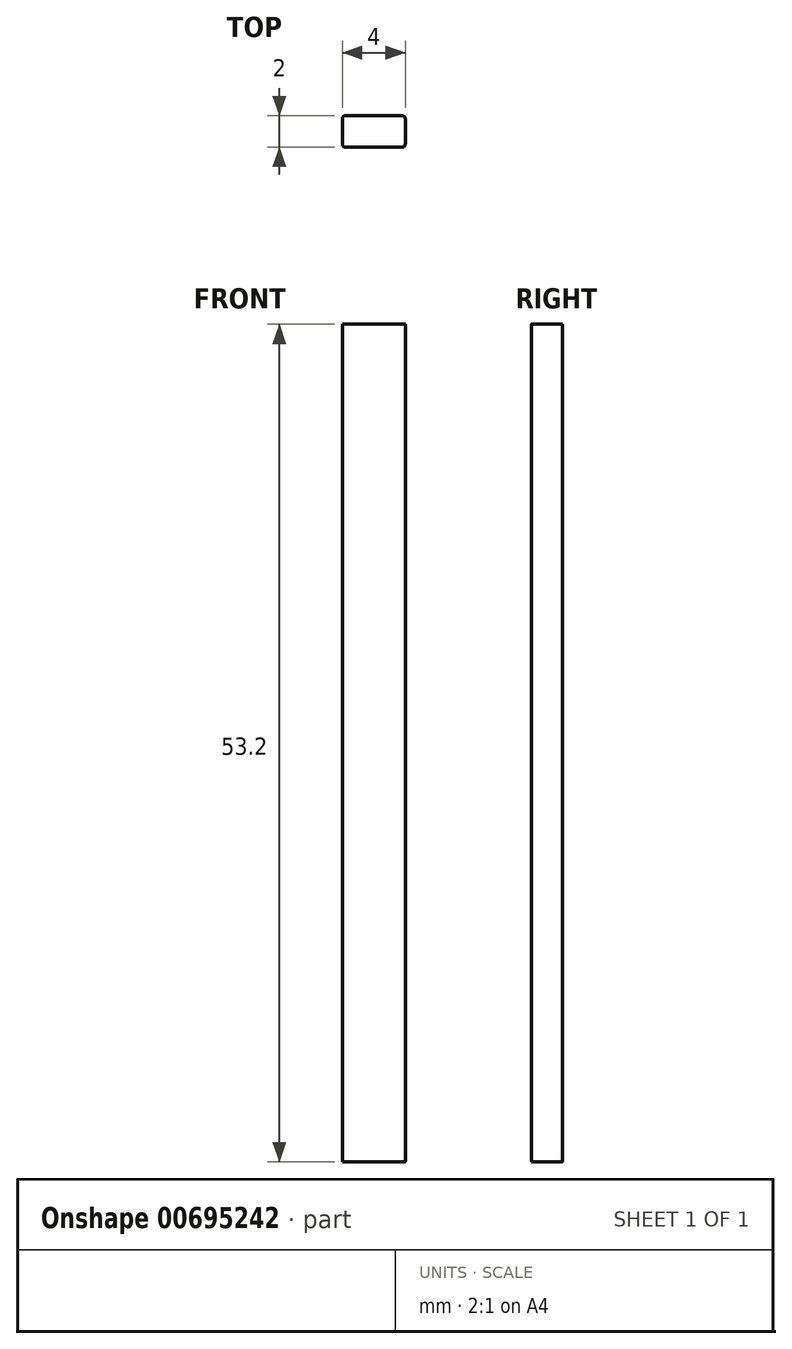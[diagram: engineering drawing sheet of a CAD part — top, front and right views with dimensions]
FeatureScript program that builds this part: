
annotation { "Feature Type Name" : "Feature", "Feature Type Description" : "" }
export const myFeature = defineFeature(function(context is Context, id is Id, definition is map)
    precondition{}
    {
        {
            var Q0;
            Q0=qCreatedBy(makeId("Top.planeOp"),FACE);
            var sketch = newSketch(context, id + "F0", { "sketchPlane" : qUnion([Q0])});
            skLineSegment(sketch, "E0.bottom", {"start": v(2, -1) * mm, "end": v(-2, -1) * mm});
            skLineSegment(sketch, "E0.top", {"start": v(2, 1) * mm, "end": v(-2, 1) * mm});
            skLineSegment(sketch, "E0.left", {"start": v(2, -1) * mm, "end": v(2, 1) * mm});
            skLineSegment(sketch, "E0.right", {"start": v(-2, -1) * mm, "end": v(-2, 1) * mm});
            skPoint(sketch, "E0.middle", {"position": v(0, 0) * mm});
            skSolve(sketch);
        }
        {
            var Q0;
            Q0 = qSketchRegion(id + "F0", true);
            extrude(context, id + "F1", {"entities" : qUnion([Q0]), "depth" : 53.2 * mm, "offsetDistance" : 25 * mm});
        }
        {
            var Q0;
            Q0=makeQuery(id+"F1.opExtrude","SWEPT_EDGE",EDGE,{"disambiguationData":[OSD([sQuery(id+"F0.wireOp",EDGE,"E0.top"),sQuery(id+"F0.wireOp",EDGE,"E0.right")])]});
            var Q1;
            Q1=makeQuery(id+"F1.opExtrude","SWEPT_EDGE",EDGE,{"disambiguationData":[OSD([sQuery(id+"F0.wireOp",EDGE,"E0.bottom"),sQuery(id+"F0.wireOp",EDGE,"E0.right")])]});
            var Q2;
            Q2=makeQuery(id+"F1.opExtrude","SWEPT_EDGE",EDGE,{"disambiguationData":[OSD([sQuery(id+"F0.wireOp",EDGE,"E0.top"),sQuery(id+"F0.wireOp",EDGE,"E0.left")])]});
            var Q3;
            Q3=makeQuery(id+"F1.opExtrude","SWEPT_EDGE",EDGE,{"disambiguationData":[OSD([sQuery(id+"F0.wireOp",EDGE,"E0.bottom"),sQuery(id+"F0.wireOp",EDGE,"E0.left")])]});
            fillet(context, id + "F2", {"entities" : qUnion([Q0, Q1, Q2, Q3]), "radius" : 0.2 * mm, "tangentPropagation" : true, "allowEdgeOverflow" : false});
        }
    });
